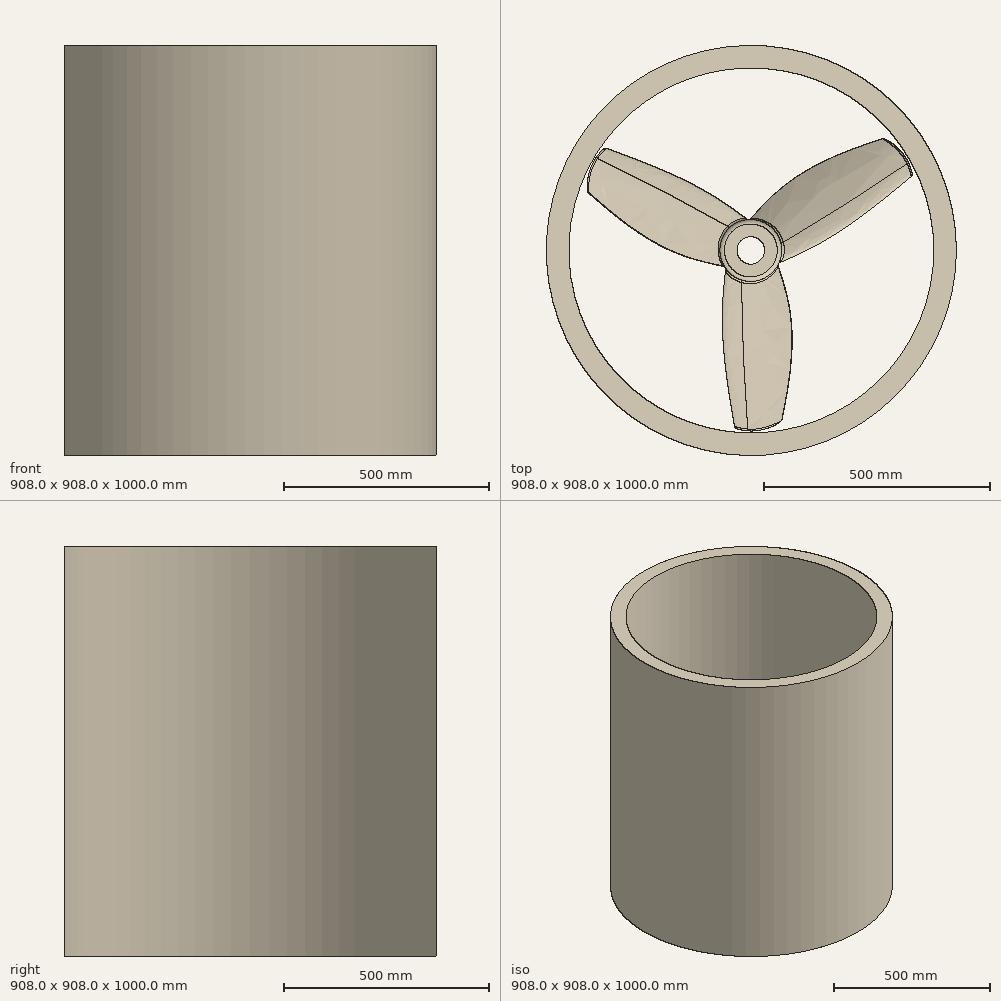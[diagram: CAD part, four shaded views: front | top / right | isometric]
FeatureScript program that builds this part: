
annotation { "Feature Type Name" : "Feature", "Feature Type Description" : "" }
export const myFeature = defineFeature(function(context is Context, id is Id, definition is map)
    precondition{}
    {
        {
            var Q0;
            Q0=qCreatedBy(makeId("Front.planeOp"),FACE);
            var sketch = newSketch(context, id + "F0", { "sketchPlane" : qUnion([Q0])});
            skLineSegment(sketch, "E0", {"start": v(-25.68, 10.16) * mm, "end": v(0, 0) * mm, "construction": true});
            skLineSegment(sketch, "E1", {"start": v(0, 0) * mm, "end": v(25.68, -10.16) * mm, "construction": true});
            skLineSegment(sketch, "E2", {"start": v(25.68, -10.16) * mm, "end": v(51.36, -20.31) * mm, "construction": true});
            skLineSegment(sketch, "E3", {"start": v(51.36, -20.31) * mm, "end": v(77.03, -30.47) * mm, "construction": true});
            skLineSegment(sketch, "E4", {"start": v(0, 0) * mm, "end": v(3.73, 9.44) * mm, "construction": true});
            skLineSegment(sketch, "E5", {"start": v(-25.68, 10.16) * mm, "end": v(-23.81, 14.88) * mm, "construction": true});
            skFitSpline(sketch, "E6", {"points": [v(-25.68, 10.16) * mm, v(3.73, 9.44) * mm, v(77.03, -30.47) * mm], "startDerivative": vector(15.03, 38) * mm, "endDerivative": vector(104.92, -93.69) * mm});
            skPoint(sketch, "E7", {"position": v(1.87, 4.72) * mm});
            skLineSegment(sketch, "E8", {"start": v(-23.81, 14.88) * mm, "end": v(1.87, 4.72) * mm, "construction": true});
            skLineSegment(sketch, "E9", {"start": v(0, 0) * mm, "end": v(-1.87, -4.72) * mm, "construction": true});
            skLineSegment(sketch, "E10", {"start": v(-25.68, 10.16) * mm, "end": v(-27.54, 5.44) * mm, "construction": true});
            skFitSpline(sketch, "E11", {"points": [v(-25.68, 10.16) * mm, v(-1.87, -4.72) * mm, v(77.03, -30.47) * mm], "startDerivative": vector(-15.23, -38.5) * mm, "endDerivative": vector(121.84, -48.19) * mm});
            skLineSegment(sketch, "E12", {"start": v(51.36, -20.31) * mm, "end": v(55.09, -10.87) * mm, "construction": true});
            skSolve(sketch);
        }
        {
            var Q0;
            Q0=qCreatedBy(makeId("Front.planeOp"),FACE);
            cPlane(context, id + "F1", {"entities" : qUnion([Q0]), "cplaneType" : CPlaneType.OFFSET, "offset" : 125 * mm, "width" : 150 * mm, "height" : 150 * mm});
        }
        {
            var Q0;
            Q0=qCreatedBy(id+"F1.planeOp",FACE);
            var sketch = newSketch(context, id + "F2", { "sketchPlane" : qUnion([Q0])});
            skLineSegment(sketch, "E13", {"start": v(-38.33, 14.06) * mm, "end": v(0, 0) * mm, "construction": true});
            skLineSegment(sketch, "E14", {"start": v(0, 0) * mm, "end": v(38.33, -14.06) * mm, "construction": true});
            skLineSegment(sketch, "E15", {"start": v(38.33, -14.06) * mm, "end": v(76.67, -28.12) * mm, "construction": true});
            skLineSegment(sketch, "E16", {"start": v(76.67, -28.12) * mm, "end": v(115, -42.17) * mm, "construction": true});
            skLineSegment(sketch, "E17", {"start": v(0, 0) * mm, "end": v(4.06, 11.06) * mm, "construction": true});
            skLineSegment(sketch, "E18", {"start": v(-38.33, 14.06) * mm, "end": v(-36.3, 19.59) * mm, "construction": true});
            skFitSpline(sketch, "E19", {"points": [v(-38.33, 14.06) * mm, v(4.06, 11.06) * mm, v(115, -42.17) * mm], "startDerivative": vector(16.44, 44.82) * mm, "endDerivative": vector(163.27, -119.63) * mm});
            skPoint(sketch, "E20", {"position": v(2.03, 5.53) * mm});
            skLineSegment(sketch, "E21", {"start": v(-36.3, 19.59) * mm, "end": v(2.03, 5.53) * mm, "construction": true});
            skLineSegment(sketch, "E22", {"start": v(0, 0) * mm, "end": v(-2.03, -5.53) * mm, "construction": true});
            skLineSegment(sketch, "E23", {"start": v(-38.33, 14.06) * mm, "end": v(-40.36, 8.53) * mm, "construction": true});
            skFitSpline(sketch, "E24", {"points": [v(-38.33, 14.06) * mm, v(-2.03, -5.53) * mm, v(115, -42.17) * mm], "startDerivative": vector(-16.57, -45.19) * mm, "endDerivative": vector(181.7, -66.64) * mm});
            skLineSegment(sketch, "E25", {"start": v(76.67, -28.12) * mm, "end": v(80.72, -17.06) * mm, "construction": true});
            skSolve(sketch);
        }
        {
            var Q0;
            Q0=qCreatedBy(makeId("Front.planeOp"),FACE);
            cPlane(context, id + "F3", {"entities" : qUnion([Q0]), "cplaneType" : CPlaneType.OFFSET, "offset" : 400 * mm, "width" : 150 * mm, "height" : 150 * mm});
        }
        {
            var Q0;
            Q0=qCreatedBy(id+"F3.planeOp",FACE);
            var sketch = newSketch(context, id + "F4", { "sketchPlane" : qUnion([Q0])});
            skLineSegment(sketch, "E26", {"start": v(-10.03, 5.14) * mm, "end": v(16.27, 0) * mm, "construction": true});
            skLineSegment(sketch, "E27", {"start": v(16.27, 0) * mm, "end": v(42.56, -5.14) * mm, "construction": true});
            skLineSegment(sketch, "E28", {"start": v(42.56, -5.14) * mm, "end": v(68.86, -10.28) * mm, "construction": true});
            skLineSegment(sketch, "E29", {"start": v(68.86, -10.28) * mm, "end": v(95.16, -15.42) * mm, "construction": true});
            skLineSegment(sketch, "E30", {"start": v(16.27, 0) * mm, "end": v(17.61, 6.9) * mm, "construction": true});
            skLineSegment(sketch, "E31", {"start": v(-10.03, 5.14) * mm, "end": v(-9.36, 8.59) * mm, "construction": true});
            skFitSpline(sketch, "E32", {"points": [v(-10.03, 5.14) * mm, v(17.61, 6.9) * mm, v(95.16, -15.42) * mm], "startDerivative": vector(5.47, 28.01) * mm, "endDerivative": vector(118.7, -57.28) * mm});
            skPoint(sketch, "E33", {"position": v(16.94, 3.45) * mm});
            skLineSegment(sketch, "E34", {"start": v(-9.36, 8.59) * mm, "end": v(16.94, 3.45) * mm, "construction": true});
            skLineSegment(sketch, "E35", {"start": v(16.27, 0) * mm, "end": v(15.6, -3.45) * mm, "construction": true});
            skLineSegment(sketch, "E36", {"start": v(-10.03, 5.14) * mm, "end": v(-10.7, 1.7) * mm, "construction": true});
            skFitSpline(sketch, "E37", {"points": [v(-10.03, 5.14) * mm, v(15.6, -3.45) * mm, v(95.16, -15.42) * mm], "startDerivative": vector(-5.51, -28.2) * mm, "endDerivative": vector(124.61, -24.36) * mm});
            skLineSegment(sketch, "E38", {"start": v(68.86, -10.28) * mm, "end": v(70.2, -3.38) * mm, "construction": true});
            skSolve(sketch);
        }
        {
            var Q0;
            Q0=qSketchRegion(id+"F0",true);
            var Q1;
            Q1=qSketchRegion(id+"F2",true);
            var Q2;
            Q2=qSketchRegion(id+"F4",true);
            var Q3;
            Q3=sQuery(id+"F0.wireOp",VERTEX,"E6.1.internal");
            var Q4;
            Q4=sQuery(id+"F2.wireOp",VERTEX,"E19.1.internal");
            var Q5;
            Q5=sQuery(id+"F4.wireOp",VERTEX,"E30.end");
            loft(context, id + "F5", {"sheetProfilesArray" : [{ "sheetProfileEntities" : qUnion([Q0]) }, { "sheetProfileEntities" : qUnion([Q1]) }, { "sheetProfileEntities" : qUnion([Q2]) }], "matchConnections" : true, "connections" : [{ "connectionEntities" : qUnion([Q3, Q4, Q5]), "connectionEdgeQueries" : qUnion([]), "connectionEdgeParameters" : [] }]});
        }
        {
            var Q0;
            Q0=qCreatedBy(makeId("Top.planeOp"),FACE);
            var sketch = newSketch(context, id + "F6", { "sketchPlane" : qUnion([Q0])});
            skFitSpline(sketch, "E39", {"points": [v(-55.98, -360.47) * mm, v(39.38, -398.87) * mm, v(142.8, -333.19) * mm], "startDerivative": vector(111.22, -150.8) * mm, "endDerivative": vector(54.24, 145.78) * mm});
            skLineSegment(sketch, "E40", {"start": v(-55.98, -360.47) * mm, "end": v(-55.98, -458.75) * mm});
            skLineSegment(sketch, "E41", {"start": v(142.8, -333.19) * mm, "end": v(142.8, -458.75) * mm});
            skLineSegment(sketch, "E42", {"start": v(142.8, -458.75) * mm, "end": v(-55.98, -458.75) * mm});
            skSolve(sketch);
        }
        {
            var Q0;
            Q0=qSketchRegion(id+"F6",true);
            extrude(context, id + "F7", {"entities" : qUnion([Q0]), "operationType" : NewBodyOperationType.REMOVE, "endBound" : BoundingType.SYMMETRIC, "oppositeDirection" : true, "depth" : 40.17 * mm});
        }
        {
            var Q0;
            Q0=makeQuery(id+"F5.opLoft","SWEPT_EDGE",EDGE,{"disambiguationData":[OSD([sQuery(id+"F2.wireOp",EDGE,"E19"),sQuery(id+"F2.wireOp",EDGE,"E24"),sQuery(id+"F4.wireOp",EDGE,"E32"),sQuery(id+"F4.wireOp",EDGE,"E37")])]});
            fillet(context, id + "F8", {"entities" : qUnion([Q0]), "radius" : 1 * mm, "tangentPropagation" : true, "allowEdgeOverflow" : false});
        }
        {
            var Q0;
            Q0=makeQuery(id+"F7.boolean.opBoolean","COPY",FACE,{"derivedFrom":makeQuery(id+"F7.opExtrude","SWEPT_FACE",FACE,{"disambiguationData":[OSD([sQuery(id+"F6.wireOp",EDGE,"E39")])]})});
            fillet(context, id + "F9", {"entities" : qUnion([Q0]), "radius" : 4 * mm, "tangentPropagation" : true, "allowEdgeOverflow" : false});
        }
        {
            var Q0;
            Q0=qCreatedBy(makeId("Top.planeOp"),FACE);
            var sketch = newSketch(context, id + "F10", { "sketchPlane" : qUnion([Q0])});
            skCircle(sketch, "E43", {"center": v(24.35, 0) * mm, "radius": 68.6 * mm});
            skSolve(sketch);
        }
        {
            var Q0;
            Q0=qSketchRegion(id+"F10",true);
            extrude(context, id + "F11", {"entities" : qUnion([Q0]), "depth" : 32.31 * mm, "hasSecondDirection" : true, "secondDirectionOppositeDirection" : true, "secondDirectionDepth" : 40 * mm});
        }
        {
            var Q0;
            Q0=makeQuery(id+"F5.opLoft","SWEPT_BODY",BODY,{"disambiguationData":[OSD([makeQuery(id+"F0.imprint","IMPRINT",FACE,{"disambiguationData":[TD([[makeQuery(id+"F0.imprint","IMPRINT",EDGE,{"derivedFrom":sQuery(id+"F0.wireOp",EDGE,"E6")}),-1.0]])]}),sQuery(id+"F2.wireOp",EDGE,"E24"),makeQuery(id+"F4.imprint","IMPRINT",FACE,{"disambiguationData":[TD([[makeQuery(id+"F4.imprint","IMPRINT",EDGE,{"derivedFrom":sQuery(id+"F4.wireOp",EDGE,"E32")}),-1.0]])]})])]});
            var Q1;
            Q1=makeQuery(id+"F11.opExtrude","SWEPT_FACE",FACE,{"disambiguationData":[OSD([sQuery(id+"F10.wireOp",EDGE,"E43")])]});
            circularPattern(context, id + "F12", {"entities" : qUnion([Q0]), "axis" : qUnion([Q1]), "angle" : 360 * degree, "instanceCount" : 3, "equalSpace" : true});
        }
        {
            var Q0;
            Q0=makeQuery(id+"F12.opPattern","COPY",BODY,{"derivedFrom":makeQuery(id+"F5.opLoft","SWEPT_BODY",BODY,{"disambiguationData":[OSD([makeQuery(id+"F0.imprint","IMPRINT",FACE,{"disambiguationData":[TD([[makeQuery(id+"F0.imprint","IMPRINT",EDGE,{"derivedFrom":sQuery(id+"F0.wireOp",EDGE,"E6")}),-1.0]])]}),sQuery(id+"F2.wireOp",EDGE,"E24"),makeQuery(id+"F4.imprint","IMPRINT",FACE,{"disambiguationData":[TD([[makeQuery(id+"F4.imprint","IMPRINT",EDGE,{"derivedFrom":sQuery(id+"F4.wireOp",EDGE,"E32")}),-1.0]])]})])]}),"instanceName":"2"});
            var Q1;
            Q1=makeQuery(id+"F5.opLoft","SWEPT_BODY",BODY,{"disambiguationData":[OSD([makeQuery(id+"F0.imprint","IMPRINT",FACE,{"disambiguationData":[TD([[makeQuery(id+"F0.imprint","IMPRINT",EDGE,{"derivedFrom":sQuery(id+"F0.wireOp",EDGE,"E6")}),-1.0]])]}),sQuery(id+"F2.wireOp",EDGE,"E24"),makeQuery(id+"F4.imprint","IMPRINT",FACE,{"disambiguationData":[TD([[makeQuery(id+"F4.imprint","IMPRINT",EDGE,{"derivedFrom":sQuery(id+"F4.wireOp",EDGE,"E32")}),-1.0]])]})])]});
            var Q2;
            Q2=makeQuery(id+"F11.opExtrude","SWEPT_BODY",BODY,{"disambiguationData":[OSD([sQuery(id+"F10.wireOp",EDGE,"E43")])]});
            var Q3;
            Q3=makeQuery(id+"F12.opPattern","COPY",BODY,{"derivedFrom":makeQuery(id+"F5.opLoft","SWEPT_BODY",BODY,{"disambiguationData":[OSD([makeQuery(id+"F0.imprint","IMPRINT",FACE,{"disambiguationData":[TD([[makeQuery(id+"F0.imprint","IMPRINT",EDGE,{"derivedFrom":sQuery(id+"F0.wireOp",EDGE,"E6")}),-1.0]])]}),sQuery(id+"F2.wireOp",EDGE,"E24"),makeQuery(id+"F4.imprint","IMPRINT",FACE,{"disambiguationData":[TD([[makeQuery(id+"F4.imprint","IMPRINT",EDGE,{"derivedFrom":sQuery(id+"F4.wireOp",EDGE,"E32")}),-1.0]])]})])]}),"instanceName":"1"});
            var Q4;
            Q4=makeQuery(id+"F12.opPattern","COPY",BODY,{"derivedFrom":makeQuery(id+"F5.opLoft","SWEPT_BODY",BODY,{"disambiguationData":[OSD([makeQuery(id+"F0.imprint","IMPRINT",FACE,{"disambiguationData":[TD([[makeQuery(id+"F0.imprint","IMPRINT",EDGE,{"derivedFrom":sQuery(id+"F0.wireOp",EDGE,"E6")}),-1.0]])]}),sQuery(id+"F2.wireOp",EDGE,"E24"),makeQuery(id+"F4.imprint","IMPRINT",FACE,{"disambiguationData":[TD([[makeQuery(id+"F4.imprint","IMPRINT",EDGE,{"derivedFrom":sQuery(id+"F4.wireOp",EDGE,"E32")}),-1.0]])]})])]}),"instanceName":"4"});
            var Q5;
            Q5=makeQuery(id+"F12.opPattern","COPY",BODY,{"derivedFrom":makeQuery(id+"F5.opLoft","SWEPT_BODY",BODY,{"disambiguationData":[OSD([makeQuery(id+"F0.imprint","IMPRINT",FACE,{"disambiguationData":[TD([[makeQuery(id+"F0.imprint","IMPRINT",EDGE,{"derivedFrom":sQuery(id+"F0.wireOp",EDGE,"E6")}),-1.0]])]}),sQuery(id+"F2.wireOp",EDGE,"E24"),makeQuery(id+"F4.imprint","IMPRINT",FACE,{"disambiguationData":[TD([[makeQuery(id+"F4.imprint","IMPRINT",EDGE,{"derivedFrom":sQuery(id+"F4.wireOp",EDGE,"E32")}),-1.0]])]})])]}),"instanceName":"3"});
            booleanBodies(context, id + "F13", {"operationType" : BooleanOperationType.UNION, "tools" : qUnion([Q0, Q1, Q2, Q3, Q4, Q5])});
        }
        {
            var Q0;
            Q0=makeQuery(id+"F11.opExtrude","CAP_FACE",FACE,{"disambiguationData":[OSD([sQuery(id+"F10.wireOp",EDGE,"E43")])],"isStart":false});
            var sketch = newSketch(context, id + "F14", { "sketchPlane" : qUnion([Q0])});
            skCircle(sketch, "E44", {"center": v(24.35, 0) * mm, "radius": 30.45 * mm});
            skSolve(sketch);
        }
        {
            var Q0;
            Q0=qSketchRegion(id+"F14",true);
            extrude(context, id + "F15", {"entities" : qUnion([Q0]), "operationType" : NewBodyOperationType.REMOVE, "endBound" : BoundingType.THROUGH_ALL, "oppositeDirection" : true, "depth" : 25 * mm});
        }
        {
            var Q0;
            {var subQ0=sQuery(id+"F0.wireOp",VERTEX,"E6.1.internal");var subQ1=sQuery(id+"F0.wireOp",EDGE,"E6");var subQ2=sQuery(id+"F0.wireOp",EDGE,"E11");var subQ3=sQuery(id+"F2.wireOp",VERTEX,"E19.1.internal");var subQ4=sQuery(id+"F2.wireOp",EDGE,"E19");var subQ5=sQuery(id+"F2.wireOp",EDGE,"E24");Q0=makeQuery(id+"F13.opBoolean","INTERSECT",EDGE,{"derivedFrom":[makeQuery(id+"F11.opExtrude","SWEPT_FACE",FACE,{"disambiguationData":[OSD([sQuery(id+"F10.wireOp",EDGE,"E43")])]}),makeQuery(id+"F12.opPattern","COPY",FACE,{"derivedFrom":makeQuery(id+"F5.opLoft","SWEPT_FACE",FACE,{"disambiguationData":[OSD([subQ0,subQ1,subQ2,subQ3,subQ4,subQ5]),TDD([subQ0,makeQuery(id+"F0.imprint","INTERSECT",VERTEX,{"disambiguationData":[OD(0.0)],"derivedFrom":[subQ1,subQ2]}),makeQuery(id+"F0.imprint","IMPRINT",EDGE,{"derivedFrom":subQ1}),subQ3,makeQuery(id+"F2.imprint","INTERSECT",VERTEX,{"disambiguationData":[OD(0.0)],"derivedFrom":[subQ4,subQ5]}),makeQuery(id+"F2.imprint","IMPRINT",EDGE,{"derivedFrom":subQ4})])]}),"instanceName":"2"})]});}
            var Q1;
            {var subQ0=sQuery(id+"F0.wireOp",VERTEX,"E6.1.internal");var subQ1=sQuery(id+"F0.wireOp",EDGE,"E6");var subQ2=sQuery(id+"F0.wireOp",EDGE,"E11");var subQ3=sQuery(id+"F2.wireOp",VERTEX,"E19.1.internal");var subQ4=sQuery(id+"F2.wireOp",EDGE,"E19");var subQ5=sQuery(id+"F2.wireOp",EDGE,"E24");Q1=makeQuery(id+"F13.opBoolean","INTERSECT",EDGE,{"derivedFrom":[makeQuery(id+"F5.opLoft","SWEPT_FACE",FACE,{"disambiguationData":[OSD([subQ0,subQ1,subQ2,subQ3,subQ4,subQ5]),TDD([subQ0,makeQuery(id+"F0.imprint","INTERSECT",VERTEX,{"disambiguationData":[OD(1.0)],"derivedFrom":[subQ1,subQ2]}),makeQuery(id+"F0.imprint","IMPRINT",EDGE,{"derivedFrom":subQ1}),subQ3,makeQuery(id+"F2.imprint","INTERSECT",VERTEX,{"disambiguationData":[OD(1.0)],"derivedFrom":[subQ4,subQ5]}),makeQuery(id+"F2.imprint","IMPRINT",EDGE,{"derivedFrom":subQ4})])]}),makeQuery(id+"F11.opExtrude","SWEPT_FACE",FACE,{"disambiguationData":[OSD([sQuery(id+"F10.wireOp",EDGE,"E43")])]})]});}
            var Q2;
            {var subQ0=sQuery(id+"F0.wireOp",VERTEX,"E6.1.internal");var subQ1=sQuery(id+"F0.wireOp",EDGE,"E6");var subQ2=sQuery(id+"F0.wireOp",EDGE,"E11");var subQ3=sQuery(id+"F2.wireOp",VERTEX,"E19.1.internal");var subQ4=sQuery(id+"F2.wireOp",EDGE,"E19");var subQ5=sQuery(id+"F2.wireOp",EDGE,"E24");Q2=makeQuery(id+"F13.opBoolean","INTERSECT",EDGE,{"derivedFrom":[makeQuery(id+"F11.opExtrude","SWEPT_FACE",FACE,{"disambiguationData":[OSD([sQuery(id+"F10.wireOp",EDGE,"E43")])]}),makeQuery(id+"F12.opPattern","COPY",FACE,{"derivedFrom":makeQuery(id+"F5.opLoft","SWEPT_FACE",FACE,{"disambiguationData":[OSD([subQ0,subQ1,subQ2,subQ3,subQ4,subQ5]),TDD([subQ0,makeQuery(id+"F0.imprint","INTERSECT",VERTEX,{"disambiguationData":[OD(1.0)],"derivedFrom":[subQ1,subQ2]}),makeQuery(id+"F0.imprint","IMPRINT",EDGE,{"derivedFrom":subQ1}),subQ3,makeQuery(id+"F2.imprint","INTERSECT",VERTEX,{"disambiguationData":[OD(1.0)],"derivedFrom":[subQ4,subQ5]}),makeQuery(id+"F2.imprint","IMPRINT",EDGE,{"derivedFrom":subQ4})])]}),"instanceName":"1"})]});}
            var Q3;
            {var subQ0=sQuery(id+"F0.wireOp",VERTEX,"E6.1.internal");var subQ1=sQuery(id+"F0.wireOp",EDGE,"E6");var subQ2=sQuery(id+"F0.wireOp",EDGE,"E11");var subQ3=sQuery(id+"F2.wireOp",VERTEX,"E19.1.internal");var subQ4=sQuery(id+"F2.wireOp",EDGE,"E19");var subQ5=sQuery(id+"F2.wireOp",EDGE,"E24");Q3=makeQuery(id+"F13.opBoolean","INTERSECT",EDGE,{"derivedFrom":[makeQuery(id+"F11.opExtrude","SWEPT_FACE",FACE,{"disambiguationData":[OSD([sQuery(id+"F10.wireOp",EDGE,"E43")])]}),makeQuery(id+"F12.opPattern","COPY",FACE,{"derivedFrom":makeQuery(id+"F5.opLoft","SWEPT_FACE",FACE,{"disambiguationData":[OSD([subQ0,subQ1,subQ2,subQ3,subQ4,subQ5]),TDD([subQ0,makeQuery(id+"F0.imprint","INTERSECT",VERTEX,{"disambiguationData":[OD(1.0)],"derivedFrom":[subQ1,subQ2]}),makeQuery(id+"F0.imprint","IMPRINT",EDGE,{"derivedFrom":subQ1}),subQ3,makeQuery(id+"F2.imprint","INTERSECT",VERTEX,{"disambiguationData":[OD(1.0)],"derivedFrom":[subQ4,subQ5]}),makeQuery(id+"F2.imprint","IMPRINT",EDGE,{"derivedFrom":subQ4})])]}),"instanceName":"4"})]});}
            var Q4;
            {var subQ0=sQuery(id+"F0.wireOp",VERTEX,"E6.1.internal");var subQ1=sQuery(id+"F0.wireOp",EDGE,"E6");var subQ2=sQuery(id+"F0.wireOp",EDGE,"E11");var subQ3=sQuery(id+"F2.wireOp",VERTEX,"E19.1.internal");var subQ4=sQuery(id+"F2.wireOp",EDGE,"E19");var subQ5=sQuery(id+"F2.wireOp",EDGE,"E24");Q4=makeQuery(id+"F13.opBoolean","INTERSECT",EDGE,{"derivedFrom":[makeQuery(id+"F11.opExtrude","SWEPT_FACE",FACE,{"disambiguationData":[OSD([sQuery(id+"F10.wireOp",EDGE,"E43")])]}),makeQuery(id+"F12.opPattern","COPY",FACE,{"derivedFrom":makeQuery(id+"F5.opLoft","SWEPT_FACE",FACE,{"disambiguationData":[OSD([subQ0,subQ1,subQ2,subQ3,subQ4,subQ5]),TDD([subQ0,makeQuery(id+"F0.imprint","INTERSECT",VERTEX,{"disambiguationData":[OD(0.0)],"derivedFrom":[subQ1,subQ2]}),makeQuery(id+"F0.imprint","IMPRINT",EDGE,{"derivedFrom":subQ1}),subQ3,makeQuery(id+"F2.imprint","INTERSECT",VERTEX,{"disambiguationData":[OD(0.0)],"derivedFrom":[subQ4,subQ5]}),makeQuery(id+"F2.imprint","IMPRINT",EDGE,{"derivedFrom":subQ4})])]}),"instanceName":"3"})]});}
            fillet(context, id + "F16", {"entities" : qUnion([Q0, Q1, Q2, Q3, Q4]), "radius" : 5 * mm, "tangentPropagation" : true, "allowEdgeOverflow" : false});
        }
        {
            var Q0;
            Q0=makeQuery(id+"F11.opExtrude","CAP_EDGE",EDGE,{"disambiguationData":[OSD([sQuery(id+"F10.wireOp",EDGE,"E43")])],"isStart":false});
            fillet(context, id + "F17", {"entities" : qUnion([Q0]), "radius" : 10 * mm, "tangentPropagation" : true, "allowEdgeOverflow" : false});
        }
        {
            var Q0;
            Q0=qCreatedBy(makeId("Top.planeOp"),FACE);
            var sketch = newSketch(context, id + "F18", { "sketchPlane" : qUnion([Q0])});
            skCircle(sketch, "E45", {"center": v(25.42, 0) * mm, "radius": 404 * mm});
            skCircle(sketch, "E46", {"center": v(25.42, 0) * mm, "radius": 454 * mm});
            skSolve(sketch);
        }
        {
            var Q0;
            Q0=makeQuery(id+"F18.imprint","IMPRINT",FACE,{"disambiguationData":[TD([[makeQuery(id+"F18.imprint","IMPRINT",EDGE,{"derivedFrom":sQuery(id+"F18.wireOp",EDGE,"E45")}),-1.0]])]});
            extrude(context, id + "F19", {"entities" : qUnion([Q0]), "endBound" : BoundingType.SYMMETRIC, "depth" : 1000 * mm, "offsetDistance" : 25 * mm});
        }
    });
